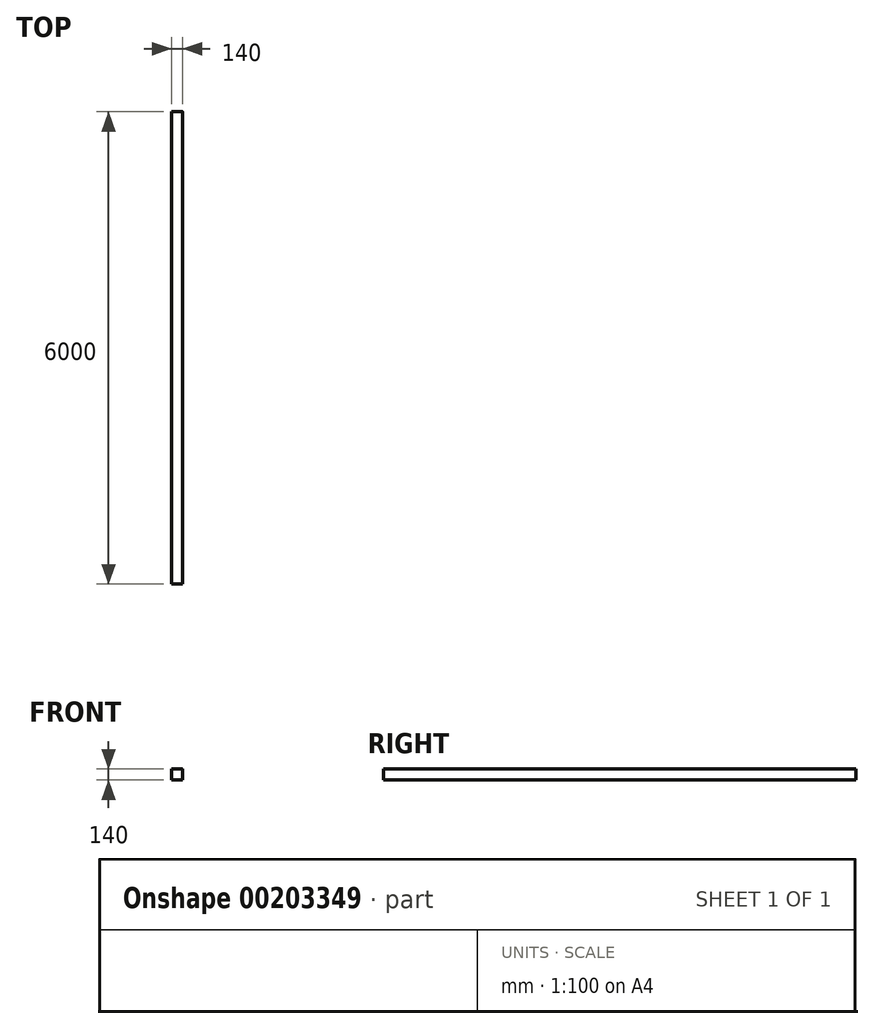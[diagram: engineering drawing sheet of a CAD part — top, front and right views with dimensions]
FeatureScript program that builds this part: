
annotation { "Feature Type Name" : "Feature", "Feature Type Description" : "" }
export const myFeature = defineFeature(function(context is Context, id is Id, definition is map)
    precondition{}
    {
        {
            var Q0;
            Q0=qCreatedBy(makeId("Front.planeOp"),FACE);
            var sketch = newSketch(context, id + "F0", { "sketchPlane" : qUnion([Q0])});
            skLineSegment(sketch, "E0.bottom", {"start": v(-70.8, 67.84) * mm, "end": v(69.2, 67.84) * mm});
            skLineSegment(sketch, "E0.top", {"start": v(-70.8, -72.16) * mm, "end": v(69.2, -72.16) * mm});
            skLineSegment(sketch, "E0.left", {"start": v(-70.8, 67.84) * mm, "end": v(-70.8, -72.16) * mm});
            skLineSegment(sketch, "E0.right", {"start": v(69.2, 67.84) * mm, "end": v(69.2, -72.16) * mm});
            skSolve(sketch);
        }
        {
            var Q0;
            Q0=makeQuery(id+"F0.imprint","IMPRINT",FACE,{"disambiguationData":[TD([[makeQuery(id+"F0.imprint","IMPRINT",EDGE,{"derivedFrom":sQuery(id+"F0.wireOp",EDGE,"E0.bottom")}),-1.0]])]});
            extrude(context, id + "F1", {"entities" : qUnion([Q0]), "depth" : 6000 * mm});
        }
        {
            var Q0;
            Q0=makeQuery(id+"F1.opExtrude","SWEPT_EDGE",EDGE,{"disambiguationData":[OSD([sQuery(id+"F0.wireOp",EDGE,"E0.bottom"),sQuery(id+"F0.wireOp",EDGE,"E0.right")])]});
            fillet(context, id + "F2", {"entities" : qUnion([Q0]), "tangentPropagation" : true, "radius" : 5 * mm, "defaultsChanged" : false, "vertexSettings" : [], "allowEdgeOverflow" : false});
        }
    });
